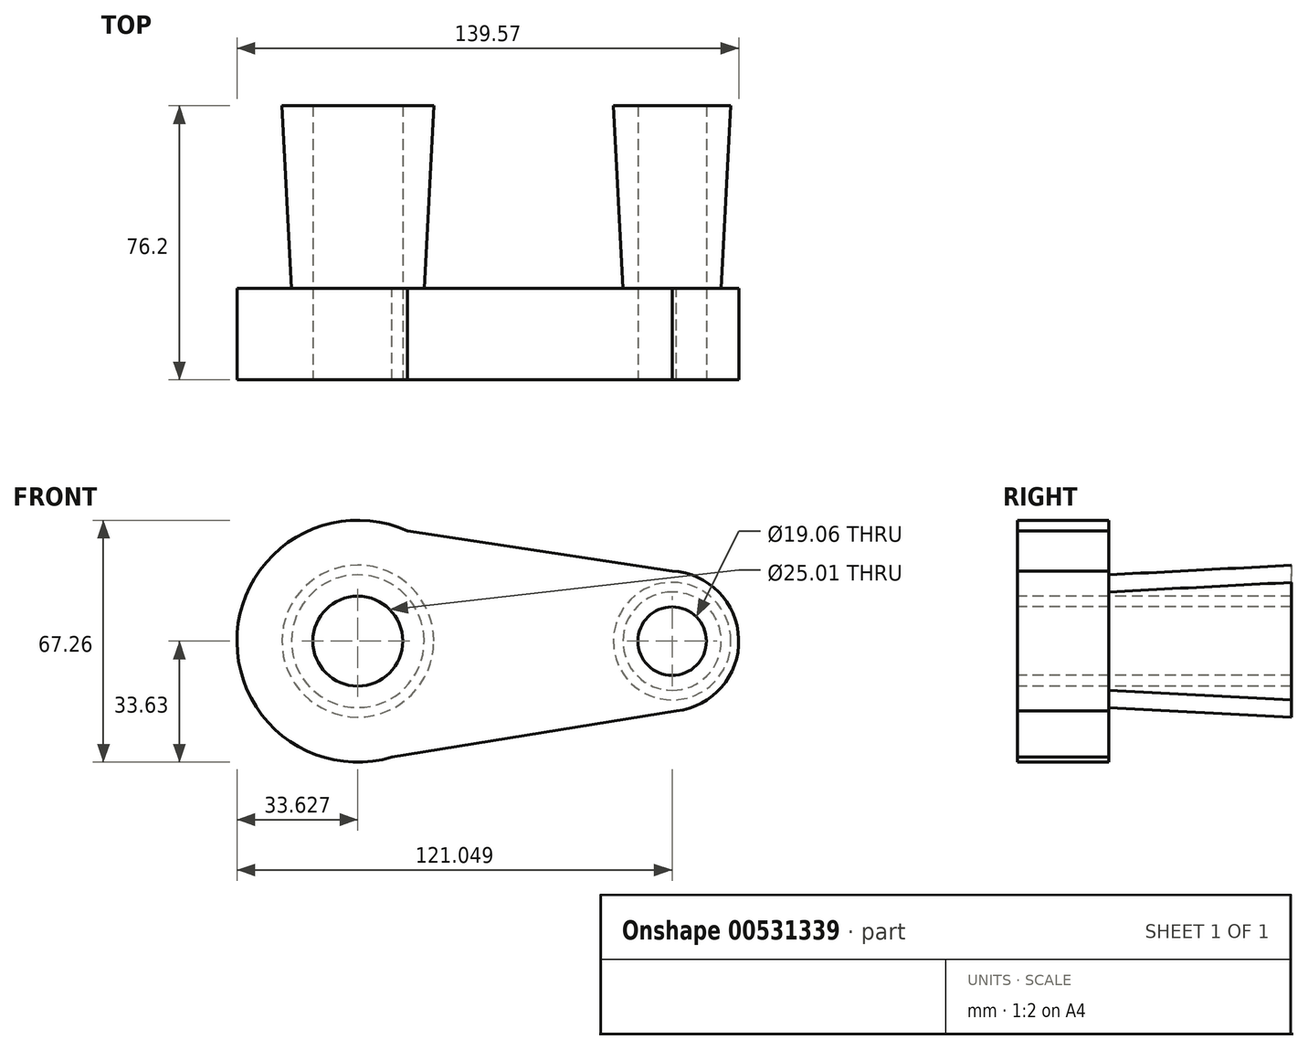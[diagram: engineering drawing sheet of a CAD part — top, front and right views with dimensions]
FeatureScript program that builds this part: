
annotation { "Feature Type Name" : "Feature", "Feature Type Description" : "" }
export const myFeature = defineFeature(function(context is Context, id is Id, definition is map)
    precondition{}
    {
        {
            var Q0;
            Q0=qCreatedBy(makeId("Front.planeOp"),FACE);
            var sketch = newSketch(context, id + "F0", { "sketchPlane" : qUnion([Q0])});
            skCircle(sketch, "E0", {"center": v(43.1, 0) * mm, "radius": 19.5 * mm});
            skCircle(sketch, "E1", {"center": v(-43.34, 0) * mm, "radius": 33.63 * mm});
            skLineSegment(sketch, "E2", {"start": v(-47.46, 33.38) * mm, "end": v(44.08, 19.48) * mm});
            skLineSegment(sketch, "E3", {"start": v(45.27, -19.38) * mm, "end": v(-42.14, -33.6) * mm});
            skSolve(sketch);
        }
        {
            var Q0;
            Q0 = qSketchRegion(id + "F0", true);
            extrude(context, id + "F1", {"entities" : qUnion([Q0]), "depth" : 25.4 * mm, "offsetDistance" : 25.4 * mm});
        }
        {
            var Q0;
            Q0=makeQuery(id+"F1.opExtrude","CAP_FACE",FACE,{"disambiguationData":[OSD([sQuery(id+"F0.wireOp",EDGE,"E0"),sQuery(id+"F0.wireOp",EDGE,"E1"),sQuery(id+"F0.wireOp",EDGE,"E2"),sQuery(id+"F0.wireOp",EDGE,"E3")])],"isStart":false});
            var sketch = newSketch(context, id + "F2", { "sketchPlane" : qUnion([Q0])});
            skCircle(sketch, "E4", {"center": v(-43.34, 0) * mm, "radius": 12.5 * mm});
            skCircle(sketch, "E5", {"center": v(44.08, 0) * mm, "radius": 9.53 * mm});
            skSolve(sketch);
        }
        {
            var Q0;
            Q0 = qSketchRegion(id + "F2", true);
            extrude(context, id + "F3", {"entities" : qUnion([Q0]), "operationType" : NewBodyOperationType.REMOVE, "oppositeDirection" : true, "depth" : 25.4 * mm, "offsetDistance" : 25.4 * mm});
        }
        {
            var Q0;
            Q0=makeQuery(id+"F1.opExtrude","CAP_FACE",FACE,{"disambiguationData":[OSD([sQuery(id+"F0.wireOp",EDGE,"E0"),sQuery(id+"F0.wireOp",EDGE,"E1"),sQuery(id+"F0.wireOp",EDGE,"E2"),sQuery(id+"F0.wireOp",EDGE,"E3")])],"isStart":true});
            var sketch = newSketch(context, id + "F4", { "sketchPlane" : qUnion([Q0])});
            skCircle(sketch, "E6", {"center": v(43.34, 0) * mm, "radius": 18.45 * mm});
            skCircle(sketch, "E7", {"center": v(-44.08, 0) * mm, "radius": 13.68 * mm});
            skSolve(sketch);
        }
        {
            var Q0;
            Q0 = qSketchRegion(id + "F4", true);
            extrude(context, id + "F5", {"entities" : qUnion([Q0]), "operationType" : NewBodyOperationType.ADD, "depth" : 50.8 * mm, "offsetDistance" : 25.4 * mm, "hasDraft" : true, "draftAngle" : 3 * degree});
        }
        {
            var Q0;
            Q0=makeQuery(id+"F5.opExtrude","CAP_FACE",FACE,{"disambiguationData":[OSD([sQuery(id+"F4.wireOp",EDGE,"E6")])],"isStart":true});
            extrude(context, id + "F6", {"entities" : qUnion([Q0]), "operationType" : NewBodyOperationType.REMOVE, "oppositeDirection" : true, "depth" : 50.8 * mm, "offsetDistance" : 25.4 * mm});
        }
        {
            var Q0;
            Q0=makeQuery(id+"F5.opExtrude","CAP_FACE",FACE,{"disambiguationData":[OSD([sQuery(id+"F4.wireOp",EDGE,"E7")])],"isStart":true});
            extrude(context, id + "F7", {"entities" : qUnion([Q0]), "operationType" : NewBodyOperationType.REMOVE, "oppositeDirection" : true, "depth" : 50.8 * mm, "offsetDistance" : 25.4 * mm});
        }
    });
